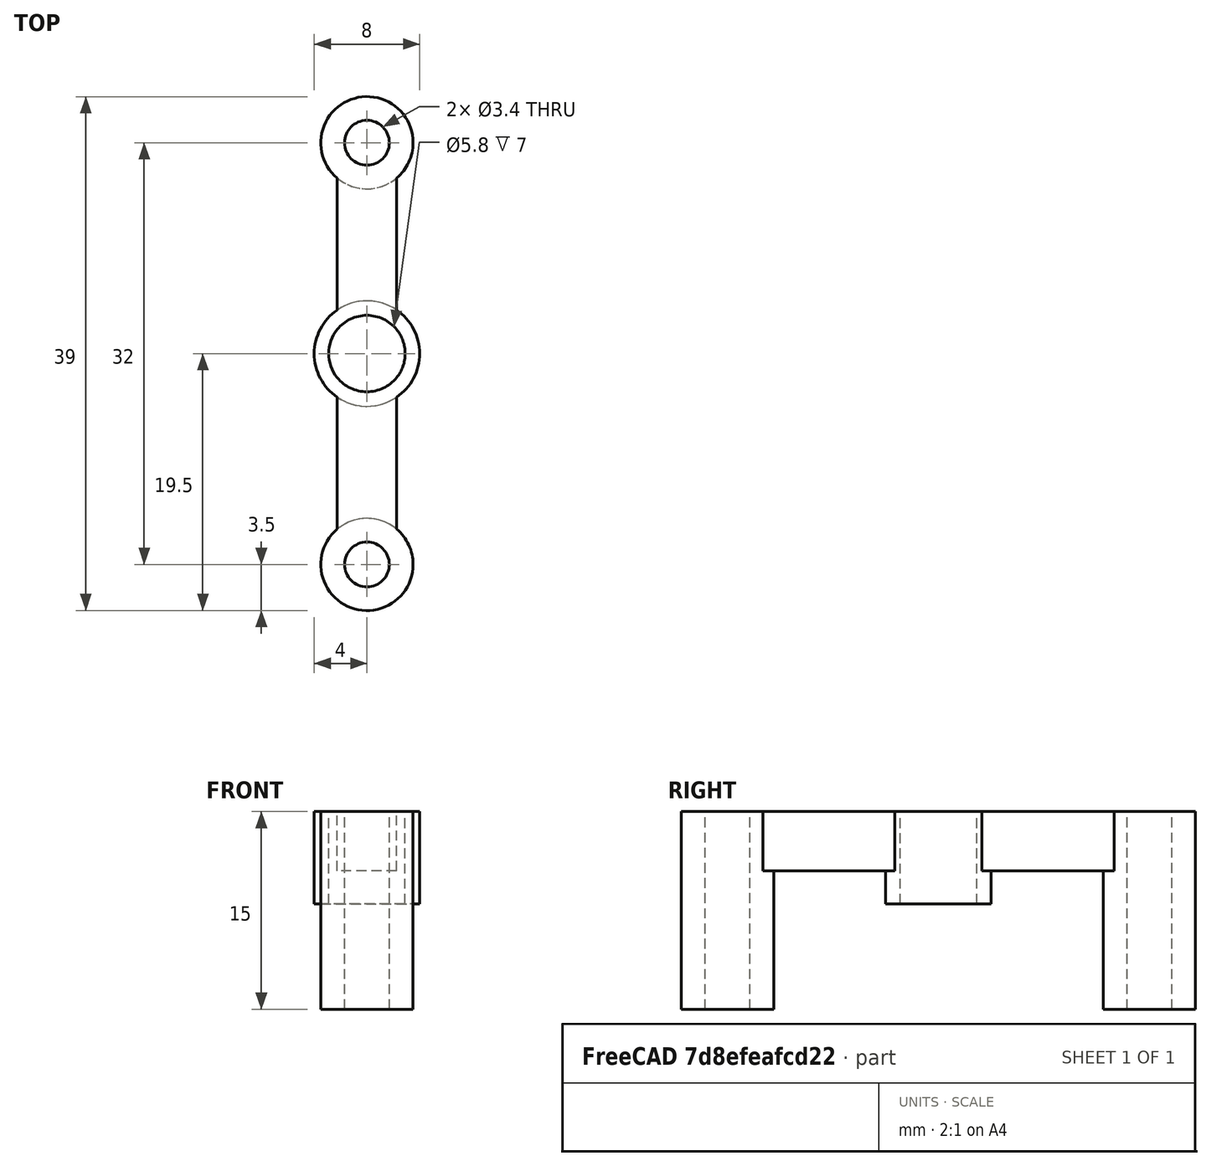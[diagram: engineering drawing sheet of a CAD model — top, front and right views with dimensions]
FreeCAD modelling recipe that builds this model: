
FCSTD DOCUMENT  (FreeCAD 0.17R11232 (Git))
Label: rough_tubing_support
License: All rights reserved
LicenseURL: http://en.wikipedia.org/wiki/All_rights_reserved
objects: Part::Cylinder×4, Part::Cut×3, Part::MultiFuse×2, Part::Box×1
note: 10 computed .brp shape members not serialized (recipe doc carries the construction recipe); baked Part::Feature solids carry a one-line shape summary decoded from their .brp

FEATURE [Part::Cylinder] Cylinder  label="leg_outer"
  Angle = 360
  AttacherType = Attacher::AttachEngine3D
  Height = 15
  Placement = pos=(0,-16,0) rot=(0,0,1;0rad)
  Radius = 3.5
FEATURE [Part::Cylinder] Cylinder001  label="leg_inner"
  Angle = 360
  AttacherType = Attacher::AttachEngine3D
  Height = 15
  Placement = pos=(0,-16,0) rot=(0,0,1;0rad)
  Radius = 1.7
FEATURE [Part::Box] Box  label="rough_arch"
  AttacherType = Attacher::AttachEngine3D
  Height = 4.5
  Length = 4.5
  Placement = pos=(-2.25,-14,10.5) rot=(0,0,1;0rad)
  Width = 28
FEATURE [Part::Cut] Cut  label="rough_leg_l"
  Base = -> Cylinder
  Tool = -> Cylinder001
FEATURE [Part::Cut] Cut001  label="rough_leg_r"
  Base = -> Cylinder
  Placement = pos=(0,32,0) rot=(0,0,1;0rad)
  Tool = -> Cylinder001
FEATURE [Part::Cylinder] Cylinder002  label="tubing_bore"
  Angle = 360
  AttacherType = Attacher::AttachEngine3D
  Height = 7
  Placement = pos=(0,0,8) rot=(0,0,1;0rad)
  Radius = 2.9
FEATURE [Part::Cylinder] Cylinder003  label="tubing_support_wall"
  Angle = 360
  AttacherType = Attacher::AttachEngine3D
  Height = 7
  Placement = pos=(0,0,8) rot=(0,0,1;0rad)
  Radius = 4
FEATURE [Part::MultiFuse] Fusion  label="arch_w_tubing_support"
  Shapes = -> [Cylinder003,Box]
FEATURE [Part::Cut] Cut002  label="center"
  Base = -> Fusion
  Tool = -> Cylinder002
FEATURE [Part::MultiFuse] Fusion001  label="rough_tubing_support"
  Shapes = -> [Cut,Cut001,Cut002]
